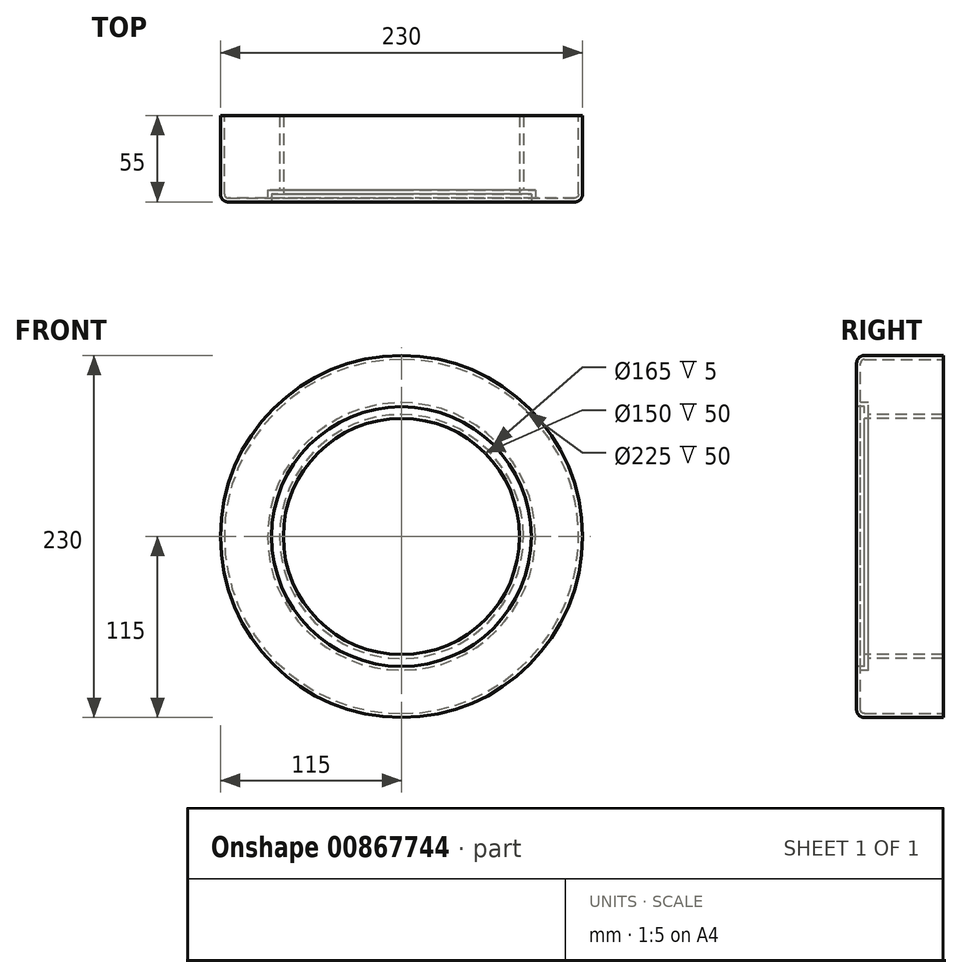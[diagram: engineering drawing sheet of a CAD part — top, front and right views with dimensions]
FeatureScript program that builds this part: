
annotation { "Feature Type Name" : "Feature", "Feature Type Description" : "" }
export const myFeature = defineFeature(function(context is Context, id is Id, definition is map)
    precondition{}
    {
        {
            var Q0;
            Q0=qCreatedBy(makeId("Front.planeOp"),FACE);
            var sketch = newSketch(context, id + "F0", { "sketchPlane" : qUnion([Q0])});
            skCircle(sketch, "E0", {"center": v(0, 0) * mm, "radius": 115 * mm});
            skSolve(sketch);
        }
        {
            var Q0;
            Q0=makeQuery(id+"F0.imprint","IMPRINT",FACE,{"disambiguationData":[TD([[makeQuery(id+"F0.imprint","IMPRINT",EDGE,{"derivedFrom":sQuery(id+"F0.wireOp",EDGE,"E0")}),1.0]])]});
            extrude(context, id + "F1", {"entities" : qUnion([Q0]), "depth" : 55 * mm, "offsetDistance" : 25 * mm});
        }
        {
            var Q0;
            Q0=makeQuery(id+"F1.opExtrude","CAP_FACE",FACE,{"disambiguationData":[OSD([sQuery(id+"F0.wireOp",EDGE,"E0")])],"isStart":false});
            var sketch = newSketch(context, id + "F2", { "sketchPlane" : qUnion([Q0])});
            skCircle(sketch, "E1", {"center": v(0, 0) * mm, "radius": 82.5 * mm});
            skCircle(sketch, "E2", {"center": v(0, 0) * mm, "radius": 75 * mm});
            skSolve(sketch);
        }
        {
            var Q0;
            Q0=makeQuery(id+"F2.imprint","IMPRINT",FACE,{"disambiguationData":[TD([[makeQuery(id+"F2.imprint","IMPRINT",EDGE,{"derivedFrom":sQuery(id+"F2.wireOp",EDGE,"E1")}),1.0]])]});
            extrude(context, id + "F3", {"entities" : qUnion([Q0]), "operationType" : NewBodyOperationType.REMOVE, "oppositeDirection" : true, "depth" : 5 * mm, "offsetDistance" : 25 * mm});
        }
        {
            var Q0;
            Q0=makeQuery(id+"F3.boolean.opBoolean","SPLIT",FACE,{"disambiguationData":[TD([makeQuery(id+"F3.opExtrude","SWEPT_FACE",FACE,{"disambiguationData":[OSD([sQuery(id+"F2.wireOp",EDGE,"E2")])]})])],"derivedFrom":makeQuery(id+"F1.opExtrude","CAP_FACE",FACE,{"disambiguationData":[OSD([sQuery(id+"F0.wireOp",EDGE,"E0")])],"isStart":false})});
            extrude(context, id + "F4", {"entities" : qUnion([Q0]), "operationType" : NewBodyOperationType.REMOVE, "oppositeDirection" : true, "depth" : 55 * mm, "offsetDistance" : 25 * mm});
        }
        {
            var Q0;
            Q0=makeQuery(id+"F3.boolean.opBoolean","COPY",EDGE,{"derivedFrom":makeQuery(id+"F3.opExtrude","CAP_EDGE",EDGE,{"disambiguationData":[OSD([sQuery(id+"F2.wireOp",EDGE,"E1")])],"isStart":true})});
            var Q1;
            Q1=makeQuery(id+"F1.opExtrude","CAP_EDGE",EDGE,{"disambiguationData":[OSD([sQuery(id+"F0.wireOp",EDGE,"E0")])],"isStart":false});
            fillet(context, id + "F5", {"entities" : qUnion([Q0, Q1]), "radius" : 5 * mm, "tangentPropagation" : true, "allowEdgeOverflow" : false});
        }
        {
            var Q0;
            Q0=makeQuery(id+"F1.opExtrude","CAP_FACE",FACE,{"disambiguationData":[OSD([sQuery(id+"F0.wireOp",EDGE,"E0")])],"isStart":true});
            shell(context, id + "F6", {"entities" : qUnion([Q0]), "thickness" : 2.5 * mm});
        }
    });
